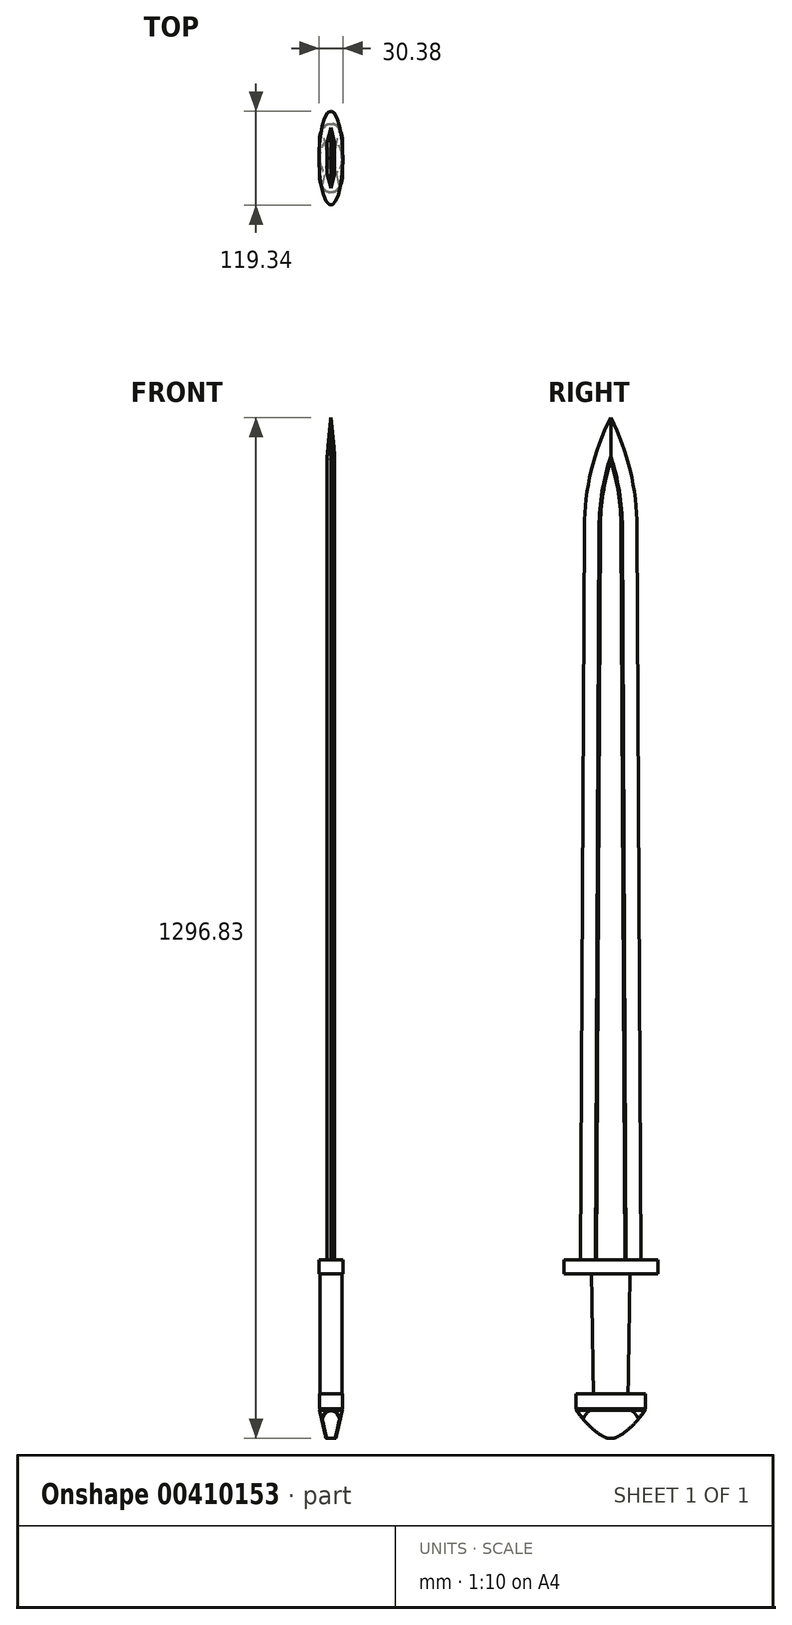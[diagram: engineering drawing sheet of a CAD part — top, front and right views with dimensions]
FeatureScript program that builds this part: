
annotation { "Feature Type Name" : "Feature", "Feature Type Description" : "" }
export const myFeature = defineFeature(function(context is Context, id is Id, definition is map)
    precondition{}
    {
        {
            var Q0;
            Q0=qCreatedBy(makeId("Top.planeOp"),FACE);
            var sketch = newSketch(context, id + "F0", { "sketchPlane" : qUnion([Q0])});
            skEllipse(sketch, "E0", {"center": v(0, 0) * mm, "majorRadius": 22.01 * mm, "minorRadius": 14.03 * mm, "majorAxis": v(0, 1)});
            skSolve(sketch);
        }
        {
            var Q0;
            Q0=makeQuery(id+"F0.imprint","IMPRINT",FACE,{"disambiguationData":[TD([[makeQuery(id+"F0.imprint","IMPRINT",EDGE,{"derivedFrom":sQuery(id+"F0.wireOp",EDGE,"E0")}),1.0]])]});
            cPlane(context, id + "F1", {"entities" : qUnion([Q0]), "cplaneType" : CPlaneType.OFFSET, "offset" : 152.4 * mm, "width" : 152.4 * mm, "height" : 152.4 * mm});
        }
        {
            var Q0;
            Q0=qCreatedBy(id+"F1.planeOp",FACE);
            var sketch = newSketch(context, id + "F2", { "sketchPlane" : qUnion([Q0])});
            skEllipse(sketch, "E1", {"center": v(0, 0) * mm, "majorRadius": 24.49 * mm, "minorRadius": 14.02 * mm, "majorAxis": v(0, 1)});
            skSolve(sketch);
        }
        {
            var Q0;
            Q0=makeQuery(id+"F0.imprint","IMPRINT",FACE,{"disambiguationData":[TD([[makeQuery(id+"F0.imprint","IMPRINT",EDGE,{"derivedFrom":sQuery(id+"F0.wireOp",EDGE,"E0")}),1.0]])]});
            var Q1;
            Q1=makeQuery(id+"F2.imprint","IMPRINT",FACE,{"disambiguationData":[TD([[makeQuery(id+"F2.imprint","IMPRINT",EDGE,{"derivedFrom":sQuery(id+"F2.wireOp",EDGE,"E1")}),1.0]])]});
            loft(context, id + "F3", {"sheetProfilesArray" : [{ "sheetProfileEntities" : qUnion([Q0]) }, { "sheetProfileEntities" : qUnion([Q1]) }]});
        }
        {
            var Q0;
            Q0=makeQuery(id+"F3.opLoft","CAP_FACE",FACE,{"disambiguationData":[OSD([makeQuery(id+"F2.imprint","IMPRINT",FACE,{"disambiguationData":[TD([[makeQuery(id+"F2.imprint","IMPRINT",EDGE,{"derivedFrom":sQuery(id+"F2.wireOp",EDGE,"E1")}),1.0]])]})])],"isStart":true});
            var sketch = newSketch(context, id + "F4", { "sketchPlane" : qUnion([Q0])});
            skEllipse(sketch, "E2", {"center": v(0, 0) * mm, "majorRadius": 50.25 * mm, "minorRadius": 14.05 * mm, "majorAxis": v(0, 1)});
            skEllipse(sketch, "E3", {"center": v(0, 0) * mm, "majorRadius": 59.67 * mm, "minorRadius": 15.2 * mm, "majorAxis": v(0, 1)});
            skSolve(sketch);
        }
        {
            var Q0;
            Q0=qSketchRegion(id+"F4",true);
            var Q1;
            Q1=makeQuery(id+"F4.imprint","IMPRINT",FACE,{"disambiguationData":[TD([[makeQuery(id+"F4.imprint","IMPRINT",EDGE,{"derivedFrom":sQuery(id+"F4.wireOp",EDGE,"E2")}),1.0]])]});
            var Q2;
            Q2=makeQuery(id+"F4.imprint","IMPRINT",FACE,{"disambiguationData":[TD([[makeQuery(id+"F4.imprint","IMPRINT",EDGE,{"derivedFrom":makeQuery(id+"F3.opLoft","MID_CAP_EDGE",EDGE,{"disambiguationData":[OSD([sQuery(id+"F0.wireOp",EDGE,"E0"),sQuery(id+"F2.wireOp",EDGE,"E1")])],"capPos":1.0})}),1.0]])]});
            extrude(context, id + "F5", {"entities" : qUnion([Q0, Q1, Q2]), "depth" : 17.78 * mm});
        }
        {
            var Q0;
            Q0=makeQuery(id+"F3.opLoft","CAP_FACE",FACE,{"disambiguationData":[OSD([makeQuery(id+"F0.imprint","IMPRINT",FACE,{"disambiguationData":[TD([[makeQuery(id+"F0.imprint","IMPRINT",EDGE,{"derivedFrom":sQuery(id+"F0.wireOp",EDGE,"E0")}),1.0]])]})])],"isStart":true});
            var sketch = newSketch(context, id + "F6", { "sketchPlane" : qUnion([Q0])});
            skLineSegment(sketch, "E4.rect.left", {"start": v(-14.65, 22.86) * mm, "end": v(-14.65, -22.86) * mm});
            skLineSegment(sketch, "E4.rect.right", {"start": v(14.65, 22.86) * mm, "end": v(14.65, -22.86) * mm});
            skPoint(sketch, "E4.rect.middle", {"position": v(0, 0) * mm});
            skPoint(sketch, "E5.rect.middle", {"position": v(-14.65, 22.86) * mm});
            skEllipticalArc(sketch, "E6", {});
            skLineSegment(sketch, "E7", {"start": v(0, 0) * mm, "end": v(-5.94, 0) * mm});
            skEllipticalArc(sketch, "E8.MirrorCS", {});
            skPoint(sketch, "E5.rect.right.end.orphan", {"position": v(-43.96, 22.86) * mm});
            skPoint(sketch, "E5.rect.right.start.orphan", {"position": v(-47.78, 25.4) * mm});
            skPoint(sketch, "E5.rect.left.end.orphan", {"position": v(18.47, 20.32) * mm});
            const initialGuessF6  = {"E6": [0, 0.02286, -1, 0, 0.014653067193173231, 0.021324570960949005, 3.141592653589793, 6.283185307179586], "E8.MirrorCS": [0, -0.02286, -1, 0, 0.014653067193173231, 0.021324570960949005, 6.283185307179586, 3.141592653589793]};
            skSetInitialGuess(sketch, initialGuessF6);
            skSolve(sketch);
        }
        {
            var Q0;
            Q0=qSketchRegion(id+"F6",true);
            extrude(context, id + "F7", {"entities" : qUnion([Q0]), "depth" : 20.32 * mm});
        }
        {
            var Q0;
            Q0=qCreatedBy(makeId("Right.planeOp"),FACE);
            var sketch = newSketch(context, id + "F8", { "sketchPlane" : qUnion([Q0])});
            skLineSegment(sketch, "E9.0", {"start": v(-44.18, -20.32) * mm, "end": v(-22.86, -20.32) * mm});
            skLineSegment(sketch, "E10.0", {"start": v(22.86, -20.32) * mm, "end": v(44.18, -20.32) * mm});
            skLineSegment(sketch, "E11", {"start": v(0, 0) * mm, "end": v(0, -64.5) * mm});
            skLineSegment(sketch, "E12", {"start": v(-10.54, -53.96) * mm, "end": v(-44.18, -20.32) * mm});
            skLineSegment(sketch, "E13", {"start": v(10.54, -53.96) * mm, "end": v(44.18, -20.32) * mm});
            skArc(sketch, "E14", {"start": v(-44.18, -20.32) * mm, "mid": v(-29.18, -38.96) * mm, "end": v(-10.54, -53.96) * mm});
            skArc(sketch, "E15.MirrorCS", {"start": v(44.18, -20.32) * mm, "mid": v(29.18, -38.96) * mm, "end": v(10.54, -53.96) * mm});
            skArc(sketch, "E16", {"start": v(-10.54, -53.96) * mm, "mid": v(0, -56.86) * mm, "end": v(10.54, -53.96) * mm});
            skLineSegment(sketch, "E17", {"start": v(-22.86, -20.32) * mm, "end": v(22.86, -20.32) * mm});
            skSolve(sketch);
        }
        {
            var Q0;
            Q0=qSketchRegion(id+"F8",true);
            extrude(context, id + "F9", {"entities" : qUnion([Q0]), "operationType" : NewBodyOperationType.ADD, "endBound" : BoundingType.SYMMETRIC, "depth" : 29.46 * mm});
        }
        {
            var Q0;
            Q0=qCreatedBy(makeId("Front.planeOp"),FACE);
            cPlane(context, id + "F10", {"entities" : qUnion([Q0]), "cplaneType" : CPlaneType.OFFSET, "offset" : 152.4 * mm, "width" : 152.4 * mm, "height" : 152.4 * mm});
        }
        {
            var Q0;
            Q0=qCreatedBy(id+"F10.planeOp",FACE);
            var sketch = newSketch(context, id + "F11", { "sketchPlane" : qUnion([Q0])});
            skLineSegment(sketch, "E18.0", {"start": v(14.73, -20.32) * mm, "end": v(0, -20.32) * mm});
            skLineSegment(sketch, "E19", {"start": v(17.78, -56.86) * mm, "end": v(-17.78, -56.86) * mm});
            skLineSegment(sketch, "E20.0", {"start": v(0, -20.32) * mm, "end": v(-14.73, -20.32) * mm});
            skLineSegment(sketch, "E21", {"start": v(-17.78, -56.86) * mm, "end": v(-10.55, -20.32) * mm});
            skLineSegment(sketch, "E22", {"start": v(0, -20.32) * mm, "end": v(0, -24.34) * mm});
            skLineSegment(sketch, "E23.MirrorCS", {"start": v(17.78, -56.86) * mm, "end": v(10.55, -20.32) * mm});
            skPoint(sketch, "E24", {"position": v(-7.37, -20.32) * mm});
            skLineSegment(sketch, "E25.0", {"start": v(-14.73, -20.32) * mm, "end": v(-14.73, -53.96) * mm});
            skLineSegment(sketch, "E26.0", {"start": v(-14.73, -53.96) * mm, "end": v(-14.73, -56.86) * mm});
            skLineSegment(sketch, "E27.0", {"start": v(14.73, -53.96) * mm, "end": v(14.73, -56.86) * mm});
            skLineSegment(sketch, "E28.0", {"start": v(14.73, -20.32) * mm, "end": v(14.73, -53.96) * mm});
            skLineSegment(sketch, "E29", {"start": v(-14.73, -20.32) * mm, "end": v(-6.3, -56.86) * mm});
            skLineSegment(sketch, "E30.MirrorCS", {"start": v(14.73, -20.32) * mm, "end": v(6.3, -56.86) * mm});
            skSolve(sketch);
        }
        {
            var Q0;
            {var subQ0=sQuery(id+"F11.wireOp",EDGE,"E28.0");var subQ1=sQuery(id+"F11.wireOp",EDGE,"E23.MirrorCS");var subQ2=makeQuery(id+"F11.imprint","INTERSECT",VERTEX,{"derivedFrom":[subQ1,subQ0]});Q0=makeQuery(id+"F11.imprint","IMPRINT",FACE,{"disambiguationData":[TD([[makeQuery(id+"F11.imprint","IMPRINT",EDGE,{"disambiguationData":[TD([[subQ2,-1.0]])],"derivedFrom":subQ1}),-1.0]])]});}
            var Q1;
            {var subQ1=sQuery(id+"F11.wireOp",EDGE,"E27.0");Q1=makeQuery(id+"F11.imprint","IMPRINT",FACE,{"disambiguationData":[TD([[makeQuery(id+"F11.imprint","IMPRINT",EDGE,{"derivedFrom":subQ1}),-1.0]])]});}
            var Q2;
            {var subQ0=sQuery(id+"F11.wireOp",EDGE,"E26.0");Q2=makeQuery(id+"F11.imprint","IMPRINT",FACE,{"disambiguationData":[TD([[makeQuery(id+"F11.imprint","IMPRINT",EDGE,{"derivedFrom":subQ0}),1.0]])]});}
            var Q3;
            {var subQ0=sQuery(id+"F11.wireOp",EDGE,"E25.0");var subQ1=sQuery(id+"F11.wireOp",EDGE,"E21");var subQ2=makeQuery(id+"F11.imprint","INTERSECT",VERTEX,{"derivedFrom":[subQ1,subQ0]});Q3=makeQuery(id+"F11.imprint","IMPRINT",FACE,{"disambiguationData":[TD([[makeQuery(id+"F11.imprint","IMPRINT",EDGE,{"disambiguationData":[TD([[subQ2,-1.0]])],"derivedFrom":subQ1}),1.0]])]});}
            extrude(context, id + "F12", {"entities" : qUnion([Q0, Q1, Q2, Q3]), "operationType" : NewBodyOperationType.REMOVE, "endBound" : BoundingType.THROUGH_ALL, "oppositeDirection" : true, "depth" : 25.4 * mm});
        }
        {
            var Q0;
            Q0=makeQuery(id+"F7.opExtrude","CAP_FACE",FACE,{"disambiguationData":[OSD([sQuery(id+"F6.wireOp",EDGE,"E4.rect.left"),sQuery(id+"F6.wireOp",EDGE,"E4.rect.right"),sQuery(id+"F6.wireOp",EDGE,"E6"),sQuery(id+"F6.wireOp",EDGE,"E8.MirrorCS")])],"isStart":true});
            var sketch = newSketch(context, id + "F13", { "sketchPlane" : qUnion([Q0])});
            skLineSegment(sketch, "E31.0.0", {"start": v(-14.73, -44.18) * mm, "end": v(0, -44.18) * mm});
            skEllipticalArc(sketch, "E31.0.1", {});
            skLineSegment(sketch, "E31.0.2", {"start": v(-14.65, -22.86) * mm, "end": v(-14.65, 22.86) * mm});
            skEllipticalArc(sketch, "E31.0.3", {});
            skLineSegment(sketch, "E31.0.4", {"start": v(0, 44.18) * mm, "end": v(-14.73, 44.18) * mm});
            skLineSegment(sketch, "E31.0.5", {"start": v(-14.73, 44.18) * mm, "end": v(-14.73, -44.18) * mm});
            skLineSegment(sketch, "E32.0.0", {"start": v(14.65, 22.86) * mm, "end": v(14.65, -22.86) * mm});
            skEllipticalArc(sketch, "E32.0.1", {});
            skLineSegment(sketch, "E32.0.2", {"start": v(0, -44.18) * mm, "end": v(14.73, -44.18) * mm});
            skLineSegment(sketch, "E32.0.3", {"start": v(14.73, -44.18) * mm, "end": v(14.73, 44.18) * mm});
            skLineSegment(sketch, "E32.0.4", {"start": v(14.73, 44.18) * mm, "end": v(0, 44.18) * mm});
            skEllipticalArc(sketch, "E32.0.5", {});
            skEllipticalArc(sketch, "E33.0.0", {});
            skLineSegment(sketch, "E33.0.1", {"start": v(14.65, -22.86) * mm, "end": v(14.65, 22.86) * mm});
            skEllipticalArc(sketch, "E33.0.2", {});
            skLineSegment(sketch, "E33.0.3", {"start": v(-14.65, 22.86) * mm, "end": v(-14.65, -22.86) * mm});
            const initialGuessF13  = {"E31.0.1": [0, -0.02286, 0, 1, 0.021324570960949005, 0.014653067193173231, 1.5707963267948966, 3.141592653589793], "E31.0.3": [0, 0.02286, 0, 1, 0.021324570960949005, 0.014653067193173231, 0, 1.5707963267948966], "E32.0.1": [0, -0.02286, 0, 1, 0.021324570960949005, 0.014653067193173231, 3.141592653589793, 4.71238898038469], "E32.0.5": [0, 0.02286, 0, 1, 0.021324570960949005, 0.014653067193173231, 4.71238898038469, 0], "E33.0.0": [0, -0.02286, 0, 1, 0.021324570960949005, 0.014653067193173231, 1.5707963267948966, 4.71238898038469], "E33.0.2": [0, 0.02286, 0, 1, 0.021324570960949005, 0.014653067193173231, 4.71238898038469, 1.5707963267948966]};
            skSetInitialGuess(sketch, initialGuessF13);
            skSolve(sketch);
        }
        {
            var Q0;
            {var subQ3=sQuery(id+"F13.wireOp",EDGE,"E31.0.0");Q0=makeQuery(id+"F13.imprint","IMPRINT",FACE,{"disambiguationData":[TD([[makeQuery(id+"F13.imprint","IMPRINT",EDGE,{"derivedFrom":subQ3}),1.0]])]});}
            var Q1;
            {var subQ3=sQuery(id+"F13.wireOp",EDGE,"E32.0.2");Q1=makeQuery(id+"F13.imprint","IMPRINT",FACE,{"disambiguationData":[TD([[makeQuery(id+"F13.imprint","IMPRINT",EDGE,{"derivedFrom":subQ3}),1.0]])]});}
            extrude(context, id + "F14", {"entities" : qUnion([Q0, Q1]), "operationType" : NewBodyOperationType.REMOVE, "endBound" : BoundingType.THROUGH_ALL, "oppositeDirection" : true, "depth" : 25.4 * mm});
        }
        {
            var Q0;
            Q0=makeQuery(id+"F7.opExtrude","CAP_FACE",FACE,{"disambiguationData":[OSD([sQuery(id+"F6.wireOp",EDGE,"E4.rect.left"),sQuery(id+"F6.wireOp",EDGE,"E4.rect.right"),sQuery(id+"F6.wireOp",EDGE,"E6"),sQuery(id+"F6.wireOp",EDGE,"E8.MirrorCS")])],"isStart":true});
            cPlane(context, id + "F15", {"entities" : qUnion([Q0]), "cplaneType" : CPlaneType.OFFSET, "offset" : 20.32 * mm, "oppositeDirection" : true, "width" : 152.4 * mm, "height" : 152.4 * mm});
        }
        {
            var Q0;
            Q0=qCreatedBy(id+"F15.planeOp",FACE);
            var sketch = newSketch(context, id + "F16", { "sketchPlane" : qUnion([Q0])});
            skEllipticalArc(sketch, "E34.0.0", {});
            skLineSegment(sketch, "E34.0.1", {"start": v(14.65, -22.86) * mm, "end": v(14.65, 22.86) * mm});
            skEllipticalArc(sketch, "E34.0.2", {});
            skLineSegment(sketch, "E34.0.3", {"start": v(-14.65, 22.86) * mm, "end": v(-14.65, -22.86) * mm});
            skLineSegment(sketch, "E35", {"start": v(-14.65, 22.86) * mm, "end": v(14.65, 22.86) * mm});
            skLineSegment(sketch, "E36", {"start": v(14.65, -22.86) * mm, "end": v(-14.65, -22.86) * mm});
            skPoint(sketch, "E37", {"position": v(0, 44.18) * mm});
            skPoint(sketch, "E38", {"position": v(0, -44.18) * mm});
            skEllipse(sketch, "E39", {"center": v(0, 22.86) * mm, "majorRadius": 21.32 * mm, "minorRadius": 14.65 * mm, "majorAxis": v(0, 1)});
            skEllipse(sketch, "E40", {"center": v(0, -22.86) * mm, "majorRadius": 21.32 * mm, "minorRadius": 14.65 * mm, "majorAxis": v(0, -1)});
            skPoint(sketch, "E41", {"position": v(-14.65, 0) * mm});
            const initialGuessF16  = {"E34.0.0": [0, -0.02286, 0, 1, 0.021324570960949005, 0.014653067193173231, 1.5707963267948966, 4.71238898038469], "E34.0.2": [0, 0.02286, 0, 1, 0.021324570960949005, 0.014653067193173231, 4.71238898038469, 1.5707963267948966], "E34.0.0": [0, -0.02286, 0, 1, 0.021324570960949005, 0.014653067193173231, 1.5707963267948966, 4.71238898038469], "E34.0.2": [0, 0.02286, 0, 1, 0.021324570960949005, 0.014653067193173231, 4.71238898038469, 1.5707963267948966]};
            skSetInitialGuess(sketch, initialGuessF16);
            skSolve(sketch);
        }
        {
            var Q0;
            Q0=qCreatedBy(makeId("Front.planeOp"),FACE);
            var sketch = newSketch(context, id + "F17", { "sketchPlane" : qUnion([Q0])});
            skPoint(sketch, "E42.0", {"position": v(-14.65, -20.32) * mm});
            skCircle(sketch, "E43", {"center": v(-14.65, -20.32) * mm, "radius": 0.94 * mm});
            skPoint(sketch, "E44.0", {"position": v(14.65, -20.32) * mm});
            skCircle(sketch, "E45", {"center": v(14.65, -20.32) * mm, "radius": 0.94 * mm});
            skPoint(sketch, "E46.0", {"position": v(7.02, -20.73) * mm});
            skPoint(sketch, "E47.0", {"position": v(36.33, -20.73) * mm});
            skSolve(sketch);
        }
        {
            var Q0;
            Q0=qCreatedBy(makeId("Front.planeOp"),FACE);
            cPlane(context, id + "F18", {"entities" : qUnion([Q0]), "cplaneType" : CPlaneType.OFFSET, "offset" : 22.86 * mm, "width" : 152.4 * mm, "height" : 152.4 * mm});
        }
        {
            var Q0;
            Q0=qCreatedBy(id+"F18.planeOp",FACE);
            var sketch = newSketch(context, id + "F19", { "sketchPlane" : qUnion([Q0])});
            skCircle(sketch, "E48.0", {"center": v(-14.65, -20.32) * mm, "radius": 0.94 * mm});
            skSolve(sketch);
        }
        {
            var Q0;
            Q0=qCreatedBy(id+"F18.planeOp",FACE);
            cPlane(context, id + "F20", {"entities" : qUnion([Q0]), "cplaneType" : CPlaneType.OFFSET, "offset" : 45.72 * mm, "oppositeDirection" : true, "width" : 152.4 * mm, "height" : 152.4 * mm});
        }
        {
            var Q0;
            Q0=qCreatedBy(id+"F20.planeOp",FACE);
            var sketch = newSketch(context, id + "F21", { "sketchPlane" : qUnion([Q0])});
            skCircle(sketch, "E49.0", {"center": v(-14.65, -20.32) * mm, "radius": 0.94 * mm});
            skSolve(sketch);
        }
        {
            var Q0;
            Q0=makeQuery(id+"F21.imprint","IMPRINT",FACE,{"disambiguationData":[TD([[makeQuery(id+"F21.imprint","IMPRINT",EDGE,{"derivedFrom":sQuery(id+"F21.wireOp",EDGE,"E49.0")}),1.0]])]});
            var Q1;
            Q1=sQuery(id+"F16.wireOp",EDGE,"E34.0.2");
            sweep(context, id + "F22", {"operationType" : NewBodyOperationType.REMOVE, "profiles" : qUnion([Q0]), "path" : qUnion([Q1])});
        }
        {
            var Q0;
            Q0=makeQuery(id+"F19.imprint","IMPRINT",FACE,{"disambiguationData":[TD([[makeQuery(id+"F19.imprint","IMPRINT",EDGE,{"derivedFrom":sQuery(id+"F19.wireOp",EDGE,"E48.0")}),1.0]])]});
            var Q1;
            Q1=sQuery(id+"F16.wireOp",EDGE,"E34.0.0");
            sweep(context, id + "F23", {"operationType" : NewBodyOperationType.REMOVE, "profiles" : qUnion([Q0]), "path" : qUnion([Q1])});
        }
        {
            var Q0;
            Q0=makeQuery(id+"F17.imprint","IMPRINT",FACE,{"disambiguationData":[TD([[makeQuery(id+"F17.imprint","IMPRINT",EDGE,{"derivedFrom":sQuery(id+"F17.wireOp",EDGE,"E43")}),1.0]])]});
            extrude(context, id + "F24", {"entities" : qUnion([Q0]), "operationType" : NewBodyOperationType.REMOVE, "endBound" : BoundingType.SYMMETRIC, "oppositeDirection" : true, "depth" : 254 * mm});
        }
        {
            var Q0;
            Q0=makeQuery(id+"F17.imprint","IMPRINT",FACE,{"disambiguationData":[TD([[makeQuery(id+"F17.imprint","IMPRINT",EDGE,{"derivedFrom":sQuery(id+"F17.wireOp",EDGE,"E45")}),1.0]])]});
            extrude(context, id + "F25", {"entities" : qUnion([Q0]), "operationType" : NewBodyOperationType.REMOVE, "endBound" : BoundingType.SYMMETRIC, "depth" : 254 * mm});
        }
        {
            var Q0;
            Q0=qCreatedBy(makeId("Right.planeOp"),FACE);
            var sketch = newSketch(context, id + "F26", { "sketchPlane" : qUnion([Q0])});
            skArc(sketch, "E50.0", {"start": v(10.54, -53.96) * mm, "mid": v(0, -56.86) * mm, "end": v(-10.54, -53.96) * mm});
            skLineSegment(sketch, "E51.0", {"start": v(-59.67, 170.18) * mm, "end": v(59.67, 170.18) * mm});
            skLineSegment(sketch, "E52", {"start": v(0, 170.18) * mm, "end": v(0, 1109.98) * mm});
            skLineSegment(sketch, "E53", {"start": v(38.35, 170.18) * mm, "end": v(33.47, 1100.69) * mm});
            skLineSegment(sketch, "E54.MirrorCS", {"start": v(-38.35, 170.18) * mm, "end": v(-33.47, 1100.69) * mm});
            skLineSegment(sketch, "E55", {"start": v(0, 1109.98) * mm, "end": v(0, 1239.97) * mm});
            skArc(sketch, "E56", {"start": v(33.47, 1100.69) * mm, "mid": v(24.8, 1172.27) * mm, "end": v(0, 1239.97) * mm});
            skArc(sketch, "E57.MirrorCS", {"start": v(-33.47, 1100.69) * mm, "mid": v(-24.8, 1172.27) * mm, "end": v(0, 1239.97) * mm});
            skSolve(sketch);
        }
        {
            var Q0;
            Q0=qSketchRegion(id+"F26",true);
            extrude(context, id + "F27", {"entities" : qUnion([Q0]), "endBound" : BoundingType.SYMMETRIC, "depth" : 10.16 * mm});
        }
        {
            var Q0;
            Q0=makeQuery(id+"F27.opExtrude","CAP_EDGE",EDGE,{"disambiguationData":[OSD([sQuery(id+"F26.wireOp",EDGE,"E53")])],"isStart":true});
            var Q1;
            Q1=makeQuery(id+"F27.opExtrude","CAP_EDGE",EDGE,{"disambiguationData":[OSD([sQuery(id+"F26.wireOp",EDGE,"E54.MirrorCS")])],"isStart":true});
            chamfer(context, id + "F28", {"entities" : qUnion([Q0, Q1]), "chamferType" : ChamferType.TWO_OFFSETS, "width1" : 5.08 * mm, "oppositeDirection" : false, "width2" : 20.32 * mm, "tangentPropagation" : true});
        }
        {
            var Q0;
            Q0=makeQuery(id+"F27.opExtrude","CAP_EDGE",EDGE,{"disambiguationData":[OSD([sQuery(id+"F26.wireOp",EDGE,"E54.MirrorCS")])],"isStart":false});
            var Q1;
            Q1=makeQuery(id+"F27.opExtrude","CAP_EDGE",EDGE,{"disambiguationData":[OSD([sQuery(id+"F26.wireOp",EDGE,"E53")])],"isStart":false});
            chamfer(context, id + "F29", {"entities" : qUnion([Q0, Q1]), "chamferType" : ChamferType.TWO_OFFSETS, "width1" : 5.08 * mm, "oppositeDirection" : false, "width2" : 20.32 * mm, "tangentPropagation" : true});
        }
        {
            var Q0;
            Q0=makeQuery(id+"F27.opExtrude","CAP_FACE",FACE,{"disambiguationData":[OSD([sQuery(id+"F26.wireOp",EDGE,"E51.0"),sQuery(id+"F26.wireOp",EDGE,"E53"),sQuery(id+"F26.wireOp",EDGE,"E54.MirrorCS"),sQuery(id+"F26.wireOp",EDGE,"E56"),sQuery(id+"F26.wireOp",EDGE,"E57.MirrorCS")])],"isStart":false});
            var sketch = newSketch(context, id + "F30", { "sketchPlane" : qUnion([Q0])});
            skLineSegment(sketch, "E58.0.0", {"start": v(-18.03, 170.18) * mm, "end": v(18.03, 170.18) * mm});
            skLineSegment(sketch, "E58.0.1", {"start": v(18.03, 170.18) * mm, "end": v(13.15, 1100.58) * mm});
            skArc(sketch, "E58.0.2", {"start": v(13.15, 1100.58) * mm, "mid": v(9.73, 1143.71) * mm, "end": v(0, 1185.87) * mm});
            skArc(sketch, "E58.0.3", {"start": v(0, 1185.87) * mm, "mid": v(-9.73, 1143.71) * mm, "end": v(-13.15, 1100.58) * mm});
            skLineSegment(sketch, "E58.0.4", {"start": v(-13.15, 1100.58) * mm, "end": v(-18.03, 170.18) * mm});
            skSolve(sketch);
        }
        {
            var Q0;
            Q0=qSketchRegion(id+"F30",true);
            extrude(context, id + "F31", {"entities" : qUnion([Q0]), "operationType" : NewBodyOperationType.REMOVE, "oppositeDirection" : true, "depth" : 2.54 * mm});
        }
        {
            var Q0;
            Q0=makeQuery(id+"F27.opExtrude","CAP_FACE",FACE,{"disambiguationData":[OSD([sQuery(id+"F26.wireOp",EDGE,"E51.0"),sQuery(id+"F26.wireOp",EDGE,"E53"),sQuery(id+"F26.wireOp",EDGE,"E54.MirrorCS"),sQuery(id+"F26.wireOp",EDGE,"E56"),sQuery(id+"F26.wireOp",EDGE,"E57.MirrorCS")])],"isStart":true});
            var sketch = newSketch(context, id + "F32", { "sketchPlane" : qUnion([Q0])});
            skLineSegment(sketch, "E59.0.0", {"start": v(-18.03, 170.18) * mm, "end": v(18.03, 170.18) * mm});
            skLineSegment(sketch, "E59.0.1", {"start": v(18.03, 170.18) * mm, "end": v(13.15, 1100.58) * mm});
            skArc(sketch, "E59.0.2", {"start": v(13.15, 1100.58) * mm, "mid": v(9.73, 1143.71) * mm, "end": v(0, 1185.87) * mm});
            skArc(sketch, "E59.0.3", {"start": v(0, 1185.87) * mm, "mid": v(-9.73, 1143.71) * mm, "end": v(-13.15, 1100.58) * mm});
            skLineSegment(sketch, "E59.0.4", {"start": v(-13.15, 1100.58) * mm, "end": v(-18.03, 170.18) * mm});
            skSolve(sketch);
        }
        {
            var Q0;
            Q0=qSketchRegion(id+"F32",true);
            extrude(context, id + "F33", {"entities" : qUnion([Q0]), "operationType" : NewBodyOperationType.REMOVE, "oppositeDirection" : true, "depth" : 2.54 * mm});
        }
        {
            var Q0;
            Q0=makeQuery(id+"F31.boolean.opBoolean","COPY",FACE,{"derivedFrom":makeQuery(id+"F31.opExtrude","CAP_FACE",FACE,{"disambiguationData":[OSD([sQuery(id+"F30.wireOp",EDGE,"E58.0.0"),sQuery(id+"F30.wireOp",EDGE,"E58.0.1"),sQuery(id+"F30.wireOp",EDGE,"E58.0.2"),sQuery(id+"F30.wireOp",EDGE,"E58.0.3"),sQuery(id+"F30.wireOp",EDGE,"E58.0.4")])],"isStart":false})});
            var sketch = newSketch(context, id + "F34", { "sketchPlane" : qUnion([Q0])});
            skLineSegment(sketch, "E60.0.0", {"start": v(-13.15, 1100.58) * mm, "end": v(-18.03, 170.18) * mm});
            skLineSegment(sketch, "E60.0.1", {"start": v(-18.03, 170.18) * mm, "end": v(18.03, 170.18) * mm});
            skLineSegment(sketch, "E60.0.2", {"start": v(18.03, 170.18) * mm, "end": v(13.15, 1100.58) * mm});
            skArc(sketch, "E60.0.3", {"start": v(13.15, 1100.58) * mm, "mid": v(9.73, 1143.71) * mm, "end": v(0, 1185.87) * mm});
            skArc(sketch, "E60.0.4", {"start": v(0, 1185.87) * mm, "mid": v(-9.73, 1143.71) * mm, "end": v(-13.15, 1100.58) * mm});
            skSolve(sketch);
        }
        {
            var Q0;
            Q0=qSketchRegion(id+"F34",true);
            extrude(context, id + "F35", {"entities" : qUnion([Q0]), "depth" : 1.27 * mm});
        }
        {
            var Q0;
            Q0=makeQuery(id+"F33.boolean.opBoolean","COPY",FACE,{"derivedFrom":makeQuery(id+"F33.opExtrude","CAP_FACE",FACE,{"disambiguationData":[OSD([sQuery(id+"F32.wireOp",EDGE,"E59.0.0"),sQuery(id+"F32.wireOp",EDGE,"E59.0.1"),sQuery(id+"F32.wireOp",EDGE,"E59.0.2"),sQuery(id+"F32.wireOp",EDGE,"E59.0.3"),sQuery(id+"F32.wireOp",EDGE,"E59.0.4")])],"isStart":false})});
            var sketch = newSketch(context, id + "F36", { "sketchPlane" : qUnion([Q0])});
            skLineSegment(sketch, "E61.0.0", {"start": v(-18.03, 170.18) * mm, "end": v(18.03, 170.18) * mm});
            skLineSegment(sketch, "E61.0.1", {"start": v(18.03, 170.18) * mm, "end": v(13.15, 1100.58) * mm});
            skArc(sketch, "E61.0.2", {"start": v(13.15, 1100.58) * mm, "mid": v(9.73, 1143.71) * mm, "end": v(0, 1185.87) * mm});
            skArc(sketch, "E61.0.3", {"start": v(0, 1185.87) * mm, "mid": v(-9.73, 1143.71) * mm, "end": v(-13.15, 1100.58) * mm});
            skLineSegment(sketch, "E61.0.4", {"start": v(-13.15, 1100.58) * mm, "end": v(-18.03, 170.18) * mm});
            skSolve(sketch);
        }
        {
            var Q0;
            Q0=qSketchRegion(id+"F36",true);
            extrude(context, id + "F37", {"entities" : qUnion([Q0]), "depth" : 1.27 * mm});
        }
        {
            var Q0;
            {var subQ0=sQuery(id+"F26.wireOp",EDGE,"E54.MirrorCS");Q0=makeQuery(id+"F31.boolean.opBoolean","MERGE",EDGE,{"derivedFrom":[makeQuery(id+"F29.opChamfer","BLEND_EDGE",EDGE,{"blendedFrom":[makeQuery(id+"F27.opExtrude","CAP_EDGE",EDGE,{"disambiguationData":[OSD([subQ0])],"isStart":false}),makeQuery(id+"F27.opExtrude","CAP_FACE",FACE,{"disambiguationData":[OSD([sQuery(id+"F26.wireOp",EDGE,"E51.0"),sQuery(id+"F26.wireOp",EDGE,"E53"),subQ0,sQuery(id+"F26.wireOp",EDGE,"E56"),sQuery(id+"F26.wireOp",EDGE,"E57.MirrorCS")])],"isStart":false})],"blendedInto":[makeQuery(id+"F27.opExtrude","CAP_FACE",FACE,{"disambiguationData":[OSD([sQuery(id+"F26.wireOp",EDGE,"E51.0"),sQuery(id+"F26.wireOp",EDGE,"E53"),subQ0,sQuery(id+"F26.wireOp",EDGE,"E56"),sQuery(id+"F26.wireOp",EDGE,"E57.MirrorCS")])],"isStart":false})]}),makeQuery(id+"F31.opExtrude","CAP_EDGE",EDGE,{"disambiguationData":[OSD([sQuery(id+"F30.wireOp",EDGE,"E58.0.4")])],"isStart":true})]});}
            var Q1;
            {var subQ0=sQuery(id+"F26.wireOp",EDGE,"E57.MirrorCS");Q1=makeQuery(id+"F31.boolean.opBoolean","MERGE",EDGE,{"derivedFrom":[makeQuery(id+"F29.opChamfer","BLEND_EDGE",EDGE,{"blendedFrom":[makeQuery(id+"F27.opExtrude","CAP_EDGE",EDGE,{"disambiguationData":[OSD([subQ0])],"isStart":false}),makeQuery(id+"F27.opExtrude","CAP_FACE",FACE,{"disambiguationData":[OSD([sQuery(id+"F26.wireOp",EDGE,"E51.0"),sQuery(id+"F26.wireOp",EDGE,"E53"),sQuery(id+"F26.wireOp",EDGE,"E54.MirrorCS"),sQuery(id+"F26.wireOp",EDGE,"E56"),subQ0])],"isStart":false})],"blendedInto":[makeQuery(id+"F27.opExtrude","CAP_FACE",FACE,{"disambiguationData":[OSD([sQuery(id+"F26.wireOp",EDGE,"E51.0"),sQuery(id+"F26.wireOp",EDGE,"E53"),sQuery(id+"F26.wireOp",EDGE,"E54.MirrorCS"),sQuery(id+"F26.wireOp",EDGE,"E56"),subQ0])],"isStart":false})]}),makeQuery(id+"F31.opExtrude","CAP_EDGE",EDGE,{"disambiguationData":[OSD([sQuery(id+"F30.wireOp",EDGE,"E58.0.3")])],"isStart":true})]});}
            var Q2;
            {var subQ0=sQuery(id+"F26.wireOp",EDGE,"E54.MirrorCS");Q2=makeQuery(id+"F33.boolean.opBoolean","MERGE",EDGE,{"derivedFrom":[makeQuery(id+"F28.opChamfer","BLEND_EDGE",EDGE,{"blendedFrom":[makeQuery(id+"F27.opExtrude","CAP_EDGE",EDGE,{"disambiguationData":[OSD([subQ0])],"isStart":true}),makeQuery(id+"F27.opExtrude","CAP_FACE",FACE,{"disambiguationData":[OSD([sQuery(id+"F26.wireOp",EDGE,"E51.0"),sQuery(id+"F26.wireOp",EDGE,"E53"),subQ0,sQuery(id+"F26.wireOp",EDGE,"E56"),sQuery(id+"F26.wireOp",EDGE,"E57.MirrorCS")])],"isStart":true})],"blendedInto":[makeQuery(id+"F27.opExtrude","CAP_FACE",FACE,{"disambiguationData":[OSD([sQuery(id+"F26.wireOp",EDGE,"E51.0"),sQuery(id+"F26.wireOp",EDGE,"E53"),subQ0,sQuery(id+"F26.wireOp",EDGE,"E56"),sQuery(id+"F26.wireOp",EDGE,"E57.MirrorCS")])],"isStart":true})]}),makeQuery(id+"F33.opExtrude","CAP_EDGE",EDGE,{"disambiguationData":[OSD([sQuery(id+"F32.wireOp",EDGE,"E59.0.1")])],"isStart":true})]});}
            var Q3;
            {var subQ0=sQuery(id+"F26.wireOp",EDGE,"E57.MirrorCS");Q3=makeQuery(id+"F33.boolean.opBoolean","MERGE",EDGE,{"derivedFrom":[makeQuery(id+"F28.opChamfer","BLEND_EDGE",EDGE,{"blendedFrom":[makeQuery(id+"F27.opExtrude","CAP_EDGE",EDGE,{"disambiguationData":[OSD([subQ0])],"isStart":true}),makeQuery(id+"F27.opExtrude","CAP_FACE",FACE,{"disambiguationData":[OSD([sQuery(id+"F26.wireOp",EDGE,"E51.0"),sQuery(id+"F26.wireOp",EDGE,"E53"),sQuery(id+"F26.wireOp",EDGE,"E54.MirrorCS"),sQuery(id+"F26.wireOp",EDGE,"E56"),subQ0])],"isStart":true})],"blendedInto":[makeQuery(id+"F27.opExtrude","CAP_FACE",FACE,{"disambiguationData":[OSD([sQuery(id+"F26.wireOp",EDGE,"E51.0"),sQuery(id+"F26.wireOp",EDGE,"E53"),sQuery(id+"F26.wireOp",EDGE,"E54.MirrorCS"),sQuery(id+"F26.wireOp",EDGE,"E56"),subQ0])],"isStart":true})]}),makeQuery(id+"F33.opExtrude","CAP_EDGE",EDGE,{"disambiguationData":[OSD([sQuery(id+"F32.wireOp",EDGE,"E59.0.2")])],"isStart":true})]});}
            chamfer(context, id + "F38", {"entities" : qUnion([Q0, Q1, Q2, Q3]), "width" : 1.27 * mm, "tangentPropagation" : true});
        }
        {
            var Q0;
            {var subQ0=sQuery(id+"F26.wireOp",EDGE,"E56");Q0=makeQuery(id+"F33.boolean.opBoolean","MERGE",EDGE,{"derivedFrom":[makeQuery(id+"F28.opChamfer","BLEND_EDGE",EDGE,{"blendedFrom":[makeQuery(id+"F27.opExtrude","CAP_EDGE",EDGE,{"disambiguationData":[OSD([subQ0])],"isStart":true}),makeQuery(id+"F27.opExtrude","CAP_FACE",FACE,{"disambiguationData":[OSD([sQuery(id+"F26.wireOp",EDGE,"E51.0"),sQuery(id+"F26.wireOp",EDGE,"E53"),sQuery(id+"F26.wireOp",EDGE,"E54.MirrorCS"),subQ0,sQuery(id+"F26.wireOp",EDGE,"E57.MirrorCS")])],"isStart":true})],"blendedInto":[makeQuery(id+"F27.opExtrude","CAP_FACE",FACE,{"disambiguationData":[OSD([sQuery(id+"F26.wireOp",EDGE,"E51.0"),sQuery(id+"F26.wireOp",EDGE,"E53"),sQuery(id+"F26.wireOp",EDGE,"E54.MirrorCS"),subQ0,sQuery(id+"F26.wireOp",EDGE,"E57.MirrorCS")])],"isStart":true})]}),makeQuery(id+"F33.opExtrude","CAP_EDGE",EDGE,{"disambiguationData":[OSD([sQuery(id+"F32.wireOp",EDGE,"E59.0.3")])],"isStart":true})]});}
            var Q1;
            {var subQ0=sQuery(id+"F26.wireOp",EDGE,"E53");Q1=makeQuery(id+"F33.boolean.opBoolean","MERGE",EDGE,{"derivedFrom":[makeQuery(id+"F28.opChamfer","BLEND_EDGE",EDGE,{"blendedFrom":[makeQuery(id+"F27.opExtrude","CAP_EDGE",EDGE,{"disambiguationData":[OSD([subQ0])],"isStart":true}),makeQuery(id+"F27.opExtrude","CAP_FACE",FACE,{"disambiguationData":[OSD([sQuery(id+"F26.wireOp",EDGE,"E51.0"),subQ0,sQuery(id+"F26.wireOp",EDGE,"E54.MirrorCS"),sQuery(id+"F26.wireOp",EDGE,"E56"),sQuery(id+"F26.wireOp",EDGE,"E57.MirrorCS")])],"isStart":true})],"blendedInto":[makeQuery(id+"F27.opExtrude","CAP_FACE",FACE,{"disambiguationData":[OSD([sQuery(id+"F26.wireOp",EDGE,"E51.0"),subQ0,sQuery(id+"F26.wireOp",EDGE,"E54.MirrorCS"),sQuery(id+"F26.wireOp",EDGE,"E56"),sQuery(id+"F26.wireOp",EDGE,"E57.MirrorCS")])],"isStart":true})]}),makeQuery(id+"F33.opExtrude","CAP_EDGE",EDGE,{"disambiguationData":[OSD([sQuery(id+"F32.wireOp",EDGE,"E59.0.4")])],"isStart":true})]});}
            var Q2;
            {var subQ0=sQuery(id+"F26.wireOp",EDGE,"E56");Q2=makeQuery(id+"F31.boolean.opBoolean","MERGE",EDGE,{"derivedFrom":[makeQuery(id+"F29.opChamfer","BLEND_EDGE",EDGE,{"blendedFrom":[makeQuery(id+"F27.opExtrude","CAP_EDGE",EDGE,{"disambiguationData":[OSD([subQ0])],"isStart":false}),makeQuery(id+"F27.opExtrude","CAP_FACE",FACE,{"disambiguationData":[OSD([sQuery(id+"F26.wireOp",EDGE,"E51.0"),sQuery(id+"F26.wireOp",EDGE,"E53"),sQuery(id+"F26.wireOp",EDGE,"E54.MirrorCS"),subQ0,sQuery(id+"F26.wireOp",EDGE,"E57.MirrorCS")])],"isStart":false})],"blendedInto":[makeQuery(id+"F27.opExtrude","CAP_FACE",FACE,{"disambiguationData":[OSD([sQuery(id+"F26.wireOp",EDGE,"E51.0"),sQuery(id+"F26.wireOp",EDGE,"E53"),sQuery(id+"F26.wireOp",EDGE,"E54.MirrorCS"),subQ0,sQuery(id+"F26.wireOp",EDGE,"E57.MirrorCS")])],"isStart":false})]}),makeQuery(id+"F31.opExtrude","CAP_EDGE",EDGE,{"disambiguationData":[OSD([sQuery(id+"F30.wireOp",EDGE,"E58.0.2")])],"isStart":true})]});}
            var Q3;
            {var subQ0=sQuery(id+"F26.wireOp",EDGE,"E53");Q3=makeQuery(id+"F31.boolean.opBoolean","MERGE",EDGE,{"derivedFrom":[makeQuery(id+"F29.opChamfer","BLEND_EDGE",EDGE,{"blendedFrom":[makeQuery(id+"F27.opExtrude","CAP_EDGE",EDGE,{"disambiguationData":[OSD([subQ0])],"isStart":false}),makeQuery(id+"F27.opExtrude","CAP_FACE",FACE,{"disambiguationData":[OSD([sQuery(id+"F26.wireOp",EDGE,"E51.0"),subQ0,sQuery(id+"F26.wireOp",EDGE,"E54.MirrorCS"),sQuery(id+"F26.wireOp",EDGE,"E56"),sQuery(id+"F26.wireOp",EDGE,"E57.MirrorCS")])],"isStart":false})],"blendedInto":[makeQuery(id+"F27.opExtrude","CAP_FACE",FACE,{"disambiguationData":[OSD([sQuery(id+"F26.wireOp",EDGE,"E51.0"),subQ0,sQuery(id+"F26.wireOp",EDGE,"E54.MirrorCS"),sQuery(id+"F26.wireOp",EDGE,"E56"),sQuery(id+"F26.wireOp",EDGE,"E57.MirrorCS")])],"isStart":false})]}),makeQuery(id+"F31.opExtrude","CAP_EDGE",EDGE,{"disambiguationData":[OSD([sQuery(id+"F30.wireOp",EDGE,"E58.0.1")])],"isStart":true})]});}
            chamfer(context, id + "F39", {"entities" : qUnion([Q0, Q1, Q2, Q3]), "width" : 1.27 * mm, "tangentPropagation" : true});
        }
        {
            var Q0;
            Q0=qCreatedBy(makeId("Right.planeOp"),FACE);
            var sketch = newSketch(context, id + "F40", { "sketchPlane" : qUnion([Q0])});
            skLineSegment(sketch, "E62.0", {"start": v(-18.03, 170.18) * mm, "end": v(18.03, 170.18) * mm});
            skLineSegment(sketch, "E63.0", {"start": v(-19.26, 170.18) * mm, "end": v(-38.35, 170.18) * mm});
            skLineSegment(sketch, "E64.0", {"start": v(-18.03, 170.18) * mm, "end": v(-19.26, 170.18) * mm});
            skLineSegment(sketch, "E65.0", {"start": v(19.26, 170.18) * mm, "end": v(18.03, 170.18) * mm});
            skLineSegment(sketch, "E66.0", {"start": v(38.35, 170.18) * mm, "end": v(19.26, 170.18) * mm});
            skLineSegment(sketch, "E67", {"start": v(-20.88, 170.18) * mm, "end": v(-10.86, -33.64) * mm});
            skLineSegment(sketch, "E68", {"start": v(0, 0) * mm, "end": v(0, 12.98) * mm});
            skLineSegment(sketch, "E69.MirrorCS", {"start": v(20.88, 170.18) * mm, "end": v(10.86, -33.64) * mm});
            skLineSegment(sketch, "E70", {"start": v(-10.86, -33.64) * mm, "end": v(10.86, -33.64) * mm});
            skSolve(sketch);
        }
        {
            var Q0;
            Q0=qSketchRegion(id+"F40",true);
            extrude(context, id + "F41", {"entities" : qUnion([Q0]), "operationType" : NewBodyOperationType.REMOVE, "endBound" : BoundingType.SYMMETRIC, "oppositeDirection" : true, "depth" : 7.11 * mm});
        }
        {
            var Q0;
            Q0=makeQuery(id+"F40.imprint","IMPRINT",FACE,{"disambiguationData":[TD([[makeQuery(id+"F40.imprint","IMPRINT",EDGE,{"derivedFrom":sQuery(id+"F40.wireOp",EDGE,"E62.0")}),-1.0]])]});
            extrude(context, id + "F42", {"entities" : qUnion([Q0]), "operationType" : NewBodyOperationType.ADD, "endBound" : BoundingType.SYMMETRIC, "depth" : 7.11 * mm});
        }
        {
            var Q0;
            Q0=makeQuery(id+"F9.opExtrude","SWEPT_FACE",FACE,{"disambiguationData":[OSD([sQuery(id+"F8.wireOp",EDGE,"E15.MirrorCS")])]});
            var Q1;
            Q1=makeQuery(id+"F9.opExtrude","SWEPT_FACE",FACE,{"disambiguationData":[OSD([sQuery(id+"F8.wireOp",EDGE,"E14")])]});
            var Q2;
            Q2=makeQuery(id+"F9.opExtrude","SWEPT_FACE",FACE,{"disambiguationData":[OSD([sQuery(id+"F8.wireOp",EDGE,"E16")])]});
            fillet(context, id + "F43", {"entities" : qUnion([Q0, Q1, Q2]), "radius" : 1.27 * mm, "tangentPropagation" : true, "allowEdgeOverflow" : false});
        }
    });
